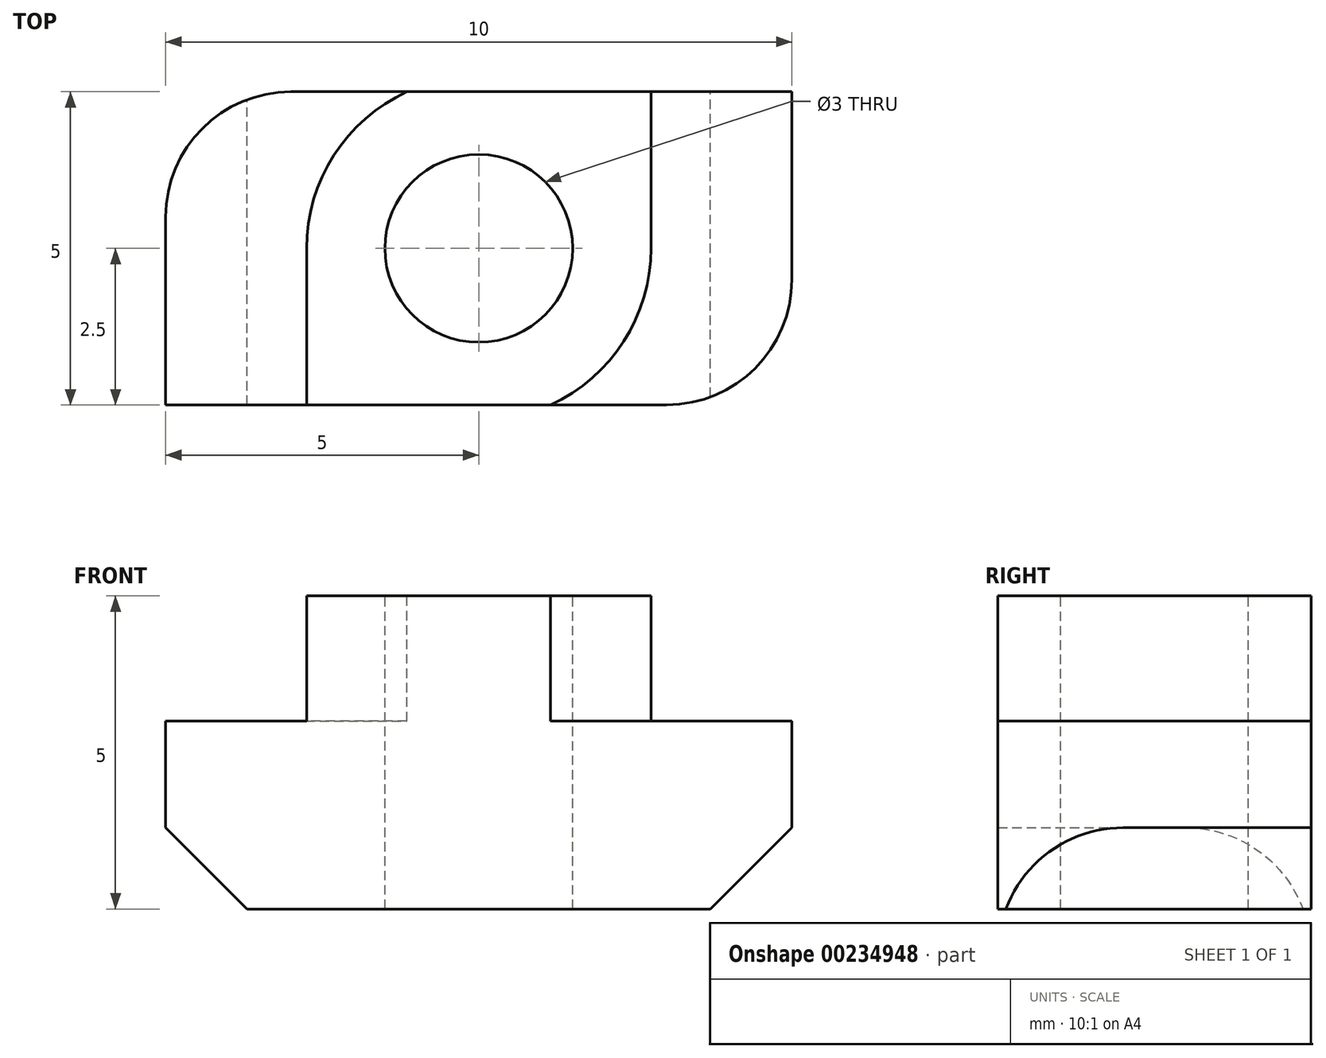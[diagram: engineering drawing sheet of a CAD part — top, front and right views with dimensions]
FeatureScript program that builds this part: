
annotation { "Feature Type Name" : "Feature", "Feature Type Description" : "" }
export const myFeature = defineFeature(function(context is Context, id is Id, definition is map)
    precondition{}
    {
        {
            var Q0;
            Q0=qCreatedBy(makeId("Front.planeOp"),FACE);
            var sketch = newSketch(context, id + "F0", { "sketchPlane" : qUnion([Q0])});
            skLineSegment(sketch, "E0", {"start": v(0, 0) * mm, "end": v(-3.7, 0) * mm});
            skLineSegment(sketch, "E1", {"start": v(-3.7, 0) * mm, "end": v(-5, 1.3) * mm});
            skLineSegment(sketch, "E2", {"start": v(-5, 1.3) * mm, "end": v(-5, 3) * mm});
            skLineSegment(sketch, "E3", {"start": v(-2.75, 3) * mm, "end": v(-2.75, 5) * mm});
            skLineSegment(sketch, "E4", {"start": v(-2.75, 5) * mm, "end": v(0, 5) * mm});
            skLineSegment(sketch, "E5", {"start": v(-5, 3) * mm, "end": v(-2.75, 3) * mm});
            skLineSegment(sketch, "E6.MirrorCS", {"start": v(5, 1.3) * mm, "end": v(5, 3) * mm});
            skLineSegment(sketch, "E7.MirrorCS", {"start": v(0, 0) * mm, "end": v(3.7, 0) * mm});
            skLineSegment(sketch, "E8.MirrorCS", {"start": v(3.7, 0) * mm, "end": v(5, 1.3) * mm});
            skLineSegment(sketch, "E9.MirrorCS", {"start": v(2.75, 5) * mm, "end": v(0, 5) * mm});
            skLineSegment(sketch, "E10.MirrorCS", {"start": v(2.75, 3) * mm, "end": v(2.75, 5) * mm});
            skLineSegment(sketch, "E11.MirrorCS", {"start": v(5, 3) * mm, "end": v(2.75, 3) * mm});
            skSolve(sketch);
        }
        {
            var Q0;
            Q0=makeQuery(id+"F0.imprint","IMPRINT",FACE,{"disambiguationData":[TD([[makeQuery(id+"F0.imprint","IMPRINT",EDGE,{"derivedFrom":sQuery(id+"F0.wireOp",EDGE,"E0")}),-1.0]])]});
            extrude(context, id + "F1", {"entities" : qUnion([Q0]), "depth" : 2.5 * mm, "hasSecondDirection" : true, "secondDirectionOppositeDirection" : true, "secondDirectionDepth" : 2.5 * mm});
        }
        {
            var Q0;
            Q0=makeQuery(id+"F1.opExtrude","SWEPT_FACE",FACE,{"disambiguationData":[OSD([sQuery(id+"F0.wireOp",EDGE,"E0"),sQuery(id+"F0.wireOp",EDGE,"E7.MirrorCS")])]});
            var sketch = newSketch(context, id + "F2", { "sketchPlane" : qUnion([Q0])});
            skCircle(sketch, "E12.cCircle", {"center": v(0, 0) * mm, "radius": 2.7 * mm, "construction": true});
            skPoint(sketch, "E12.cCircle.perimeterSnap0", {"position": v(0, 2.5) * mm});
            skLineSegment(sketch, "E12.0", {"start": v(-1.56, 2.7) * mm, "end": v(1.56, 2.7) * mm});
            skLineSegment(sketch, "E12.1", {"start": v(1.56, 2.7) * mm, "end": v(3.12, 0) * mm});
            skLineSegment(sketch, "E12.2", {"start": v(3.12, 0) * mm, "end": v(1.56, -2.7) * mm});
            skLineSegment(sketch, "E12.3", {"start": v(1.56, -2.7) * mm, "end": v(-1.56, -2.7) * mm});
            skLineSegment(sketch, "E12.4", {"start": v(-1.56, -2.7) * mm, "end": v(-3.12, 0) * mm});
            skLineSegment(sketch, "E12.5", {"start": v(-3.12, 0) * mm, "end": v(-1.56, 2.7) * mm});
            skPoint(sketch, "E12.0.midPoint", {"position": v(0, 2.7) * mm});
            skPoint(sketch, "E12.0.midPoint.positionSnap0", {"position": v(0, 2.5) * mm});
            skSolve(sketch);
        }
        {
            var Q0;
            Q0=makeQuery(id+"F1.opExtrude","SWEPT_FACE",FACE,{"disambiguationData":[OSD([sQuery(id+"F0.wireOp",EDGE,"E4"),sQuery(id+"F0.wireOp",EDGE,"E9.MirrorCS")])]});
            var sketch = newSketch(context, id + "F3", { "sketchPlane" : qUnion([Q0])});
            skCircle(sketch, "E13", {"center": v(0, 0) * mm, "radius": 1.5 * mm});
            skCircle(sketch, "E14", {"center": v(0, 0) * mm, "radius": 2.81 * mm});
            skSolve(sketch);
        }
        {
            var Q0;
            Q0=makeQuery(id+"F3.imprint","IMPRINT",FACE,{"disambiguationData":[TD([[makeQuery(id+"F3.imprint","IMPRINT",EDGE,{"derivedFrom":sQuery(id+"F3.wireOp",EDGE,"E13")}),1.0]])]});
            extrude(context, id + "F4", {"entities" : qUnion([Q0]), "operationType" : NewBodyOperationType.REMOVE, "endBound" : BoundingType.THROUGH_ALL, "oppositeDirection" : true, "depth" : 25 * mm});
        }
        {
            var Q0;
            Q0=makeQuery(id+"F1.opExtrude","SWEPT_FACE",FACE,{"disambiguationData":[OSD([sQuery(id+"F0.wireOp",EDGE,"E4"),sQuery(id+"F0.wireOp",EDGE,"E9.MirrorCS")])]});
            var sketch = newSketch(context, id + "F5", { "sketchPlane" : qUnion([Q0])});
            skCircle(sketch, "E15", {"center": v(0, 0) * mm, "radius": 2.75 * mm});
            skSolve(sketch);
        }
        {
            var Q0;
            {var subQ0=sQuery(id+"F5.wireOp",EDGE,"E15");var subQ1=sQuery(id+"F0.wireOp",EDGE,"E9.MirrorCS");var subQ2=makeQuery(id+"F1.opExtrude","SWEPT_EDGE",EDGE,{"disambiguationData":[OSD([subQ1,sQuery(id+"F0.wireOp",EDGE,"E10.MirrorCS")])]});var subQ3=makeQuery(id+"F5.imprint","INTERSECT",VERTEX,{"derivedFrom":[subQ2,subQ0]});Q0=makeQuery(id+"F5.imprint","IMPRINT",FACE,{"disambiguationData":[TD([[makeQuery(id+"F5.imprint","IMPRINT",EDGE,{"disambiguationData":[TD([[subQ3,1.0]])],"derivedFrom":subQ0}),-1.0]])]});}
            var Q1;
            {var subQ0=sQuery(id+"F5.wireOp",EDGE,"E15");var subQ1=sQuery(id+"F0.wireOp",EDGE,"E4");var subQ2=makeQuery(id+"F1.opExtrude","CAP_EDGE",EDGE,{"disambiguationData":[OSD([subQ1,sQuery(id+"F0.wireOp",EDGE,"E9.MirrorCS")])],"isStart":true});var subQ3=makeQuery(id+"F5.imprint","INTERSECT",VERTEX,{"disambiguationData":[OD(1.0)],"derivedFrom":[subQ2,subQ0]});Q1=makeQuery(id+"F5.imprint","IMPRINT",FACE,{"disambiguationData":[TD([[makeQuery(id+"F5.imprint","IMPRINT",EDGE,{"disambiguationData":[TD([[subQ3,-1.0]])],"derivedFrom":subQ0}),-1.0]])]});}
            var Q2;
            Q2=makeQuery(id+"F1.opExtrude","SWEPT_FACE",FACE,{"disambiguationData":[OSD([sQuery(id+"F0.wireOp",EDGE,"E5")])]});
            extrude(context, id + "F6", {"entities" : qUnion([Q0, Q1]), "operationType" : NewBodyOperationType.REMOVE, "endBound" : BoundingType.UP_TO_SURFACE, "oppositeDirection" : true, "endBoundEntityFace" : qUnion([Q2]), "depth" : 25 * mm});
        }
        {
            var Q0;
            Q0=makeQuery(id+"F1.opExtrude","CAP_EDGE",EDGE,{"disambiguationData":[OSD([sQuery(id+"F0.wireOp",EDGE,"E6.MirrorCS")])],"isStart":false});
            var Q1;
            Q1=makeQuery(id+"F1.opExtrude","CAP_EDGE",EDGE,{"disambiguationData":[OSD([sQuery(id+"F0.wireOp",EDGE,"E2")])],"isStart":true});
            fillet(context, id + "F7", {"entities" : qUnion([Q0, Q1]), "radius" : 2 * mm, "tangentPropagation" : true, "allowEdgeOverflow" : false});
        }
    });
